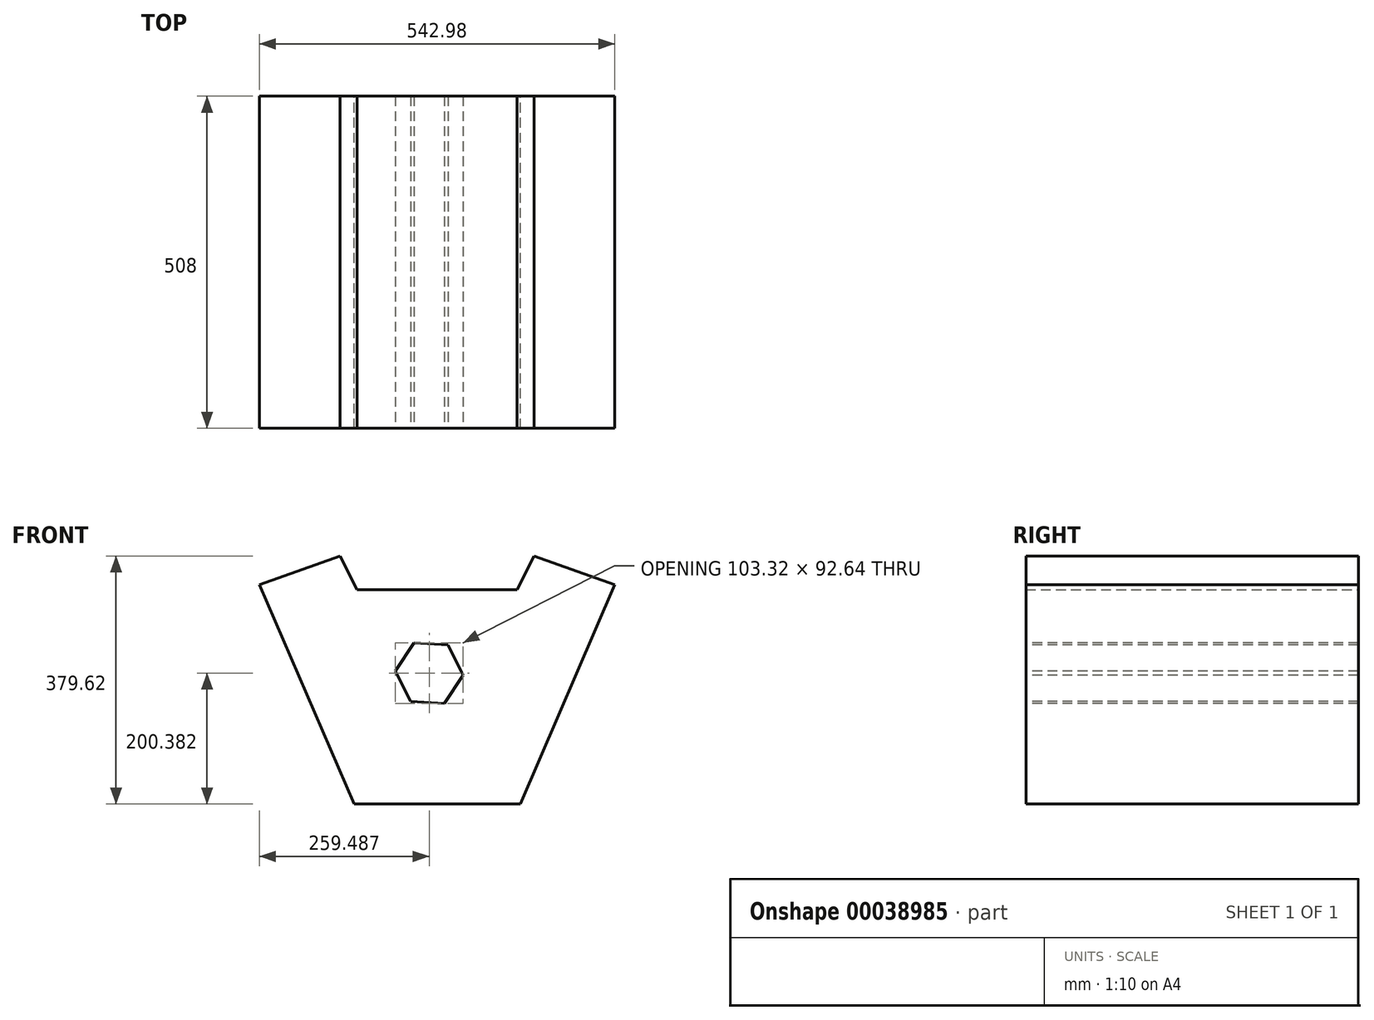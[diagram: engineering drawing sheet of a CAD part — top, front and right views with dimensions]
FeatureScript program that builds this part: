
annotation { "Feature Type Name" : "Feature", "Feature Type Description" : "" }
export const myFeature = defineFeature(function(context is Context, id is Id, definition is map)
    precondition{}
    {
        {
            var Q0;
            Q0=qCreatedBy(makeId("Front.planeOp"),FACE);
            var sketch = newSketch(context, id + "F0", { "sketchPlane" : qUnion([Q0])});
            skLineSegment(sketch, "E0", {"start": v(0, 0) * mm, "end": v(-127, 0) * mm});
            skLineSegment(sketch, "E1", {"start": v(-127, 0) * mm, "end": v(-271.49, 335.45) * mm});
            skLineSegment(sketch, "E2", {"start": v(-271.49, 335.45) * mm, "end": v(-148.17, 379.62) * mm});
            skLineSegment(sketch, "E3", {"start": v(-148.17, 379.62) * mm, "end": v(-122.4, 328.08) * mm});
            skLineSegment(sketch, "E4", {"start": v(-122.4, 328.08) * mm, "end": v(0, 328.08) * mm});
            skLineSegment(sketch, "E5.MirrorCS", {"start": v(0, 0) * mm, "end": v(127, 0) * mm});
            skLineSegment(sketch, "E6.MirrorCS", {"start": v(127, 0) * mm, "end": v(271.49, 335.45) * mm});
            skLineSegment(sketch, "E7.MirrorCS", {"start": v(122.4, 328.08) * mm, "end": v(0, 328.08) * mm});
            skLineSegment(sketch, "E8.MirrorCS", {"start": v(148.17, 379.62) * mm, "end": v(122.4, 328.08) * mm});
            skLineSegment(sketch, "E9.MirrorCS", {"start": v(271.49, 335.45) * mm, "end": v(148.17, 379.62) * mm});
            skSolve(sketch);
        }
        {
            var Q0;
            Q0 = qSketchRegion(id + "F0", true);
            extrude(context, id + "F1", {"entities" : qUnion([Q0]), "depth" : 508 * mm});
        }
        {
            var Q0;
            Q0=makeQuery(id+"F1.opExtrude","CAP_FACE",FACE,{"disambiguationData":[OSD([sQuery(id+"F0.wireOp",EDGE,"E0"),sQuery(id+"F0.wireOp",EDGE,"E1"),sQuery(id+"F0.wireOp",EDGE,"E2"),sQuery(id+"F0.wireOp",EDGE,"E3"),sQuery(id+"F0.wireOp",EDGE,"E4"),sQuery(id+"F0.wireOp",EDGE,"E5.MirrorCS"),sQuery(id+"F0.wireOp",EDGE,"E6.MirrorCS"),sQuery(id+"F0.wireOp",EDGE,"E7.MirrorCS"),sQuery(id+"F0.wireOp",EDGE,"E8.MirrorCS"),sQuery(id+"F0.wireOp",EDGE,"E9.MirrorCS")])],"isStart":false});
            var sketch = newSketch(context, id + "F2", { "sketchPlane" : qUnion([Q0])});
            skCircle(sketch, "E10.cCircle", {"center": v(-12, 200.38) * mm, "radius": 44.82 * mm, "construction": true});
            skLineSegment(sketch, "E10.0", {"start": v(16.57, 243.54) * mm, "end": v(39.66, 197.22) * mm});
            skLineSegment(sketch, "E10.1", {"start": v(39.66, 197.22) * mm, "end": v(11.09, 154.06) * mm});
            skLineSegment(sketch, "E10.2", {"start": v(11.09, 154.06) * mm, "end": v(-40.57, 157.22) * mm});
            skLineSegment(sketch, "E10.3", {"start": v(-40.57, 157.22) * mm, "end": v(-63.66, 203.54) * mm});
            skLineSegment(sketch, "E10.4", {"start": v(-63.66, 203.54) * mm, "end": v(-35.1, 246.7) * mm});
            skLineSegment(sketch, "E10.5", {"start": v(-35.1, 246.7) * mm, "end": v(16.57, 243.54) * mm});
            skPoint(sketch, "E10.0.midPoint", {"position": v(28.11, 220.38) * mm});
            skSolve(sketch);
        }
        {
            var Q0;
            Q0=makeQuery(id+"F2.imprint","IMPRINT",FACE,{"disambiguationData":[TD([[makeQuery(id+"F2.imprint","IMPRINT",EDGE,{"derivedFrom":sQuery(id+"F2.wireOp",EDGE,"E10.0")}),-1.0]])]});
            extrude(context, id + "F3", {"entities" : qUnion([Q0]), "operationType" : NewBodyOperationType.REMOVE, "endBound" : BoundingType.UP_TO_NEXT, "oppositeDirection" : true, "depth" : 302.26 * mm, "offsetDistance" : 25.4 * mm});
        }
    });
